# Revit family: LBRP-8RD
name_source: partatom
category: Lighting Fixtures
units: mm (PartAtom-declared; Revit-internal decimal feet)

## family parameters
Cut with Voids When Loaded = No
Host = Face
Light Source = Yes
OmniClass Number = 23.80.70.11.14.17
OmniClass Title = Direct/Indirect
Part Type = Normal
Room Calculation Point = No
Round Connector Dimension = Use Diameter
Shared = Yes

## types (1)
- LBRP-8RD
    A = 7.15 "
    Apparent Load = 12 VA
    Assembly Code = D5020200
    B = 9.1 "
    C = 0.2 "
    Color Filter = 16777215
    D = 6.65 "
    Default Elevation = 48 "
    Description = PRO CANLESS DIRECT INSTALL DOWNLIGHT
    Dimming Lamp Color Temperature Shift = <None>
    Emit Shape Visible in Rendering = No
    Emit from Circle Diameter = 7.5 "
    Glass = White Glass
    Heat Sink = Black
    Housing Material = Paint - Matte White
    Lamp = LED's
    Load Classification = Lighting
    Manufacturer = Prescolite Lighting
    Model = LBRP
    Photometric Notes = More IES files download on Photometric Web Link
    Photometric Web File = LBRP-M-LSHL30K9_LBRP-8RD-T-D_3000lm.IES
    Power Factor = 0.9
    Tilt Angle = -90.00°
    URL = https://www.currentlighting.com
    Voltage = 120 V
    Warranty = 5-Years Warranty
    Wattage Comments = 9.6 - 55 W
    zz Length 1 = 48 "

## geometry (parser evidence)
native form markers: Sweep x2
no freeform markers — native parametric forms only
